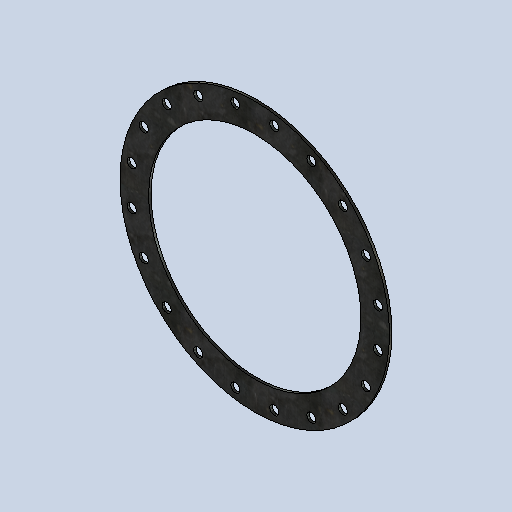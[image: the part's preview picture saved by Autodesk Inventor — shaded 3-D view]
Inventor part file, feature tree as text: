
AUTODESK INVENTOR PART (.ipt)
format: ipt  version: 2025.1 (Build 291241020, 241B)  size: 247,296 bytes
history: native  units: mm
features: sketch x2, other x2, extrude x1, pattern_circular x1, projected_geometry x1
ambient origin geometry x8: Origin, YZ Plane, XZ Plane, XY Plane, X Axis, Y Axis, Z Axis, Center Point
bodies: Solid1 (feature_tree)
feature tree (7):
  extrude  "Extrusion1"  Depth=6.0mm TaperAngle=0.0deg
  pattern_circular  "Circular Pattern1"  Count=31  [1 undecoded]
  sketch  "Sketch1"  dims[d0=512.0mm d1=670.0mm d2=6.0mm d3=0.0mm]
  sketch  "Sketch2"  dims[d4=528.0mm d5=310.0mm d7=23.0mm d8=6.0mm d9=6.0mm d10=0.0mm d11=200.0mm d12=360.0deg]
  projected_geometry  "Projected Loop1"
  other  "Cut1"
  other  "Definition1"
note: 1 required parameter value undecoded (feature->parameter linkage not recoverable at this tier; creation-order binding heuristic only, values carry confidence <= 0.55)
